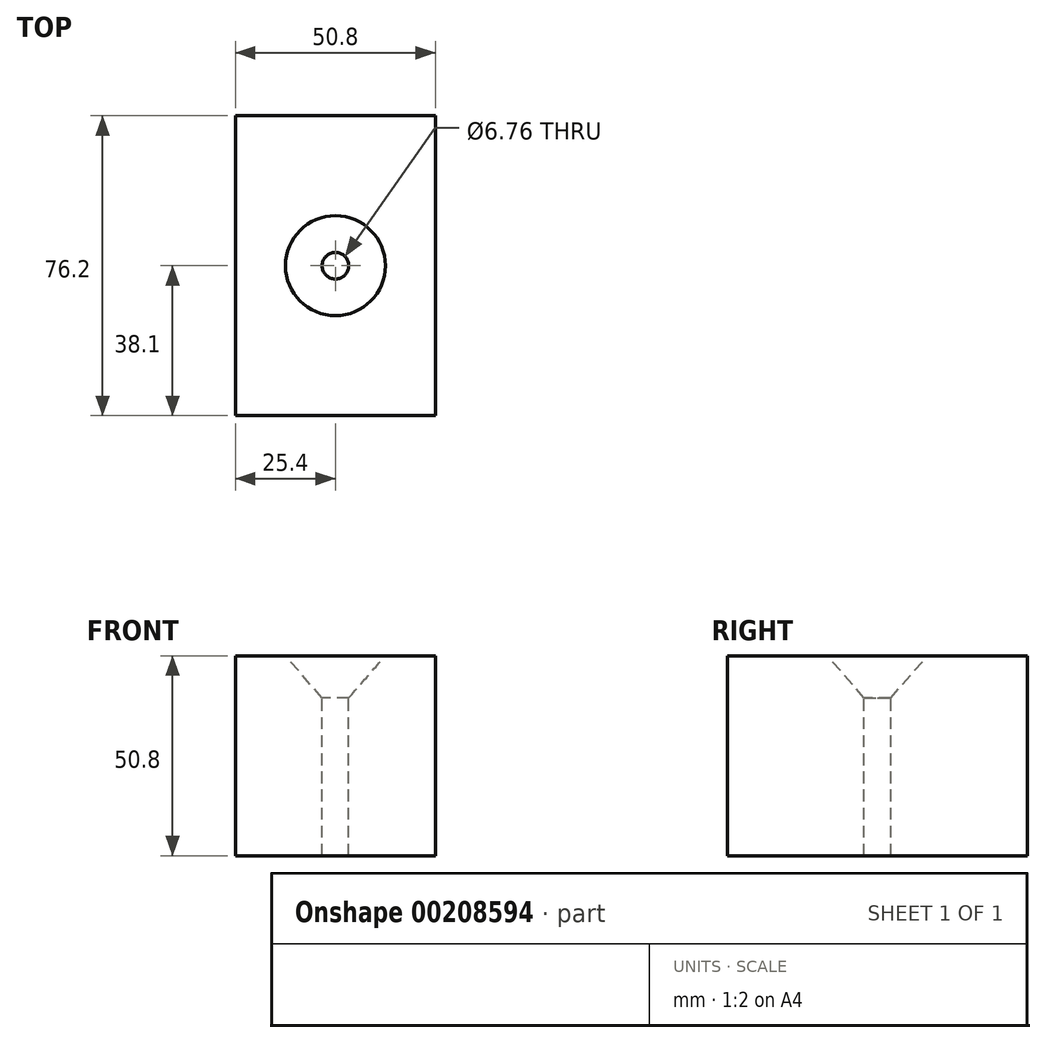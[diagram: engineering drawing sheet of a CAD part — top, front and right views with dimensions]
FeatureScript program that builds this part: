
annotation { "Feature Type Name" : "Feature", "Feature Type Description" : "" }
export const myFeature = defineFeature(function(context is Context, id is Id, definition is map)
    precondition{}
    {
        {
            var Q0;
            Q0=qCreatedBy(makeId("Front.planeOp"),FACE);
            var sketch = newSketch(context, id + "F0", { "sketchPlane" : qUnion([Q0])});
            skLineSegment(sketch, "E0.bottom", {"start": v(0, 0) * mm, "end": v(50.8, 0) * mm});
            skLineSegment(sketch, "E0.top", {"start": v(0, 50.8) * mm, "end": v(50.8, 50.8) * mm});
            skLineSegment(sketch, "E0.left", {"start": v(0, 0) * mm, "end": v(0, 50.8) * mm});
            skLineSegment(sketch, "E0.right", {"start": v(50.8, 0) * mm, "end": v(50.8, 50.8) * mm});
            skSolve(sketch);
        }
        {
            var Q0;
            Q0=makeQuery(id+"F0.imprint","IMPRINT",FACE,{"disambiguationData":[TD([[makeQuery(id+"F0.imprint","IMPRINT",EDGE,{"derivedFrom":sQuery(id+"F0.wireOp",EDGE,"E0.bottom")}),1.0]])]});
            extrude(context, id + "F1", {"entities" : qUnion([Q0]), "depth" : 76.2 * mm});
        }
        {
            var Q0;
            Q0=makeQuery(id+"F1.opExtrude","SWEPT_FACE",FACE,{"disambiguationData":[OSD([sQuery(id+"F0.wireOp",EDGE,"E0.top")])]});
            var sketch = newSketch(context, id + "F2", { "sketchPlane" : qUnion([Q0])});
            skCircle(sketch, "E1", {"center": v(25.4, -38.1) * mm, "radius": 12.7 * mm});
            skPoint(sketch, "E1.centerSnap0", {"position": v(0, -38.1) * mm});
            skPoint(sketch, "E1.centerSnap1", {"position": v(25.4, 0) * mm});
            skSolve(sketch);
        }
        {
            var Q0;
            Q0=sQuery(id+"F2.wireOp",VERTEX,"E1.center");
            var Q1;
            Q1=makeQuery(id+"F1.opExtrude","SWEPT_BODY",BODY,{"disambiguationData":[OSD([sQuery(id+"F0.wireOp",EDGE,"E0.bottom"),sQuery(id+"F0.wireOp",EDGE,"E0.top"),sQuery(id+"F0.wireOp",EDGE,"E0.left"),sQuery(id+"F0.wireOp",EDGE,"E0.right")])]});
            hole(context, id + "F3", {"style" : HoleStyle.C_SINK, "endStyle" : HoleEndStyle.THROUGH, "holeDiameter" : 6.76 * mm, "cSinkDiameter" : 25.4 * mm, "cSinkAngle" : 82 * degree, "startFromSketch" : true, "locations" : qUnion([Q0]), "scope" : qUnion([Q1]), "isTappedThrough" : true});
        }
    });
